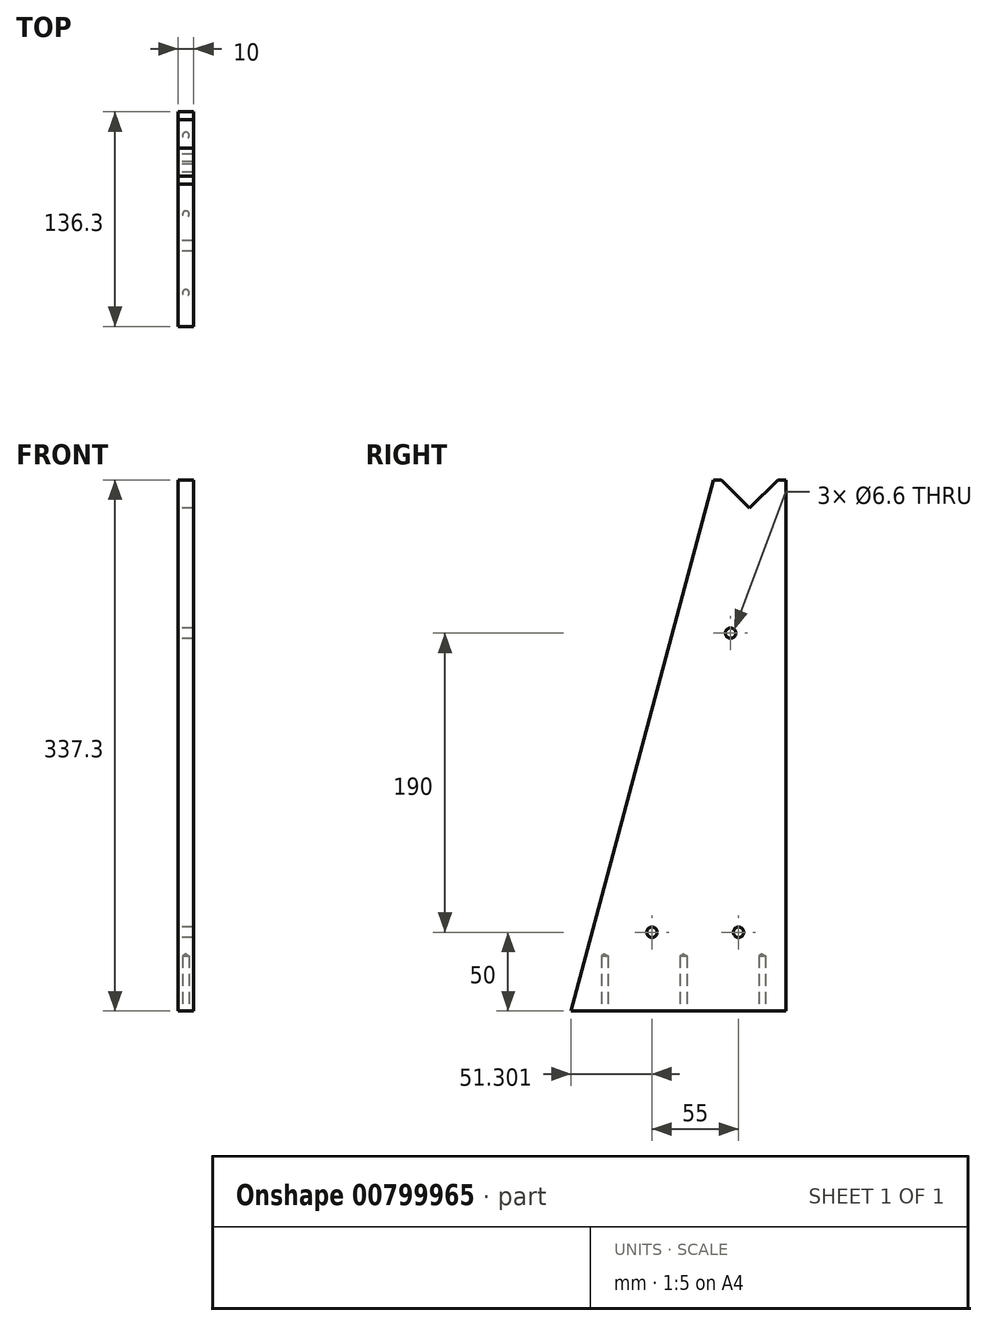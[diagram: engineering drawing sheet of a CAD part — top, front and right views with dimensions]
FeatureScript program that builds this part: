
annotation { "Feature Type Name" : "Feature", "Feature Type Description" : "" }
export const myFeature = defineFeature(function(context is Context, id is Id, definition is map)
    precondition{}
    {
        {
            var Q0;
            Q0=qCreatedBy(makeId("Right.planeOp"),FACE);
            var sketch = newSketch(context, id + "F0", { "sketchPlane" : qUnion([Q0])});
            skLineSegment(sketch, "E0.bottom", {"start": v(-90.9, 0) * mm, "end": v(45.4, 0) * mm});
            skLineSegment(sketch, "E0.right", {"start": v(45.4, 0) * mm, "end": v(45.4, 337.3) * mm});
            skLineSegment(sketch, "E1", {"start": v(22.4, 337.3) * mm, "end": v(22.4, 312.8) * mm, "construction": true});
            skLineSegment(sketch, "E2", {"start": v(22.4, 319.34) * mm, "end": v(4.44, 337.3) * mm});
            skLineSegment(sketch, "E3", {"start": v(22.4, 319.34) * mm, "end": v(40.36, 337.3) * mm});
            skCircle(sketch, "E4", {"center": v(22.4, 337.3) * mm, "radius": 12.7 * mm, "construction": true});
            skPoint(sketch, "E4.first.point", {"position": v(22.4, 350) * mm});
            skPoint(sketch, "E4.second.point", {"position": v(13.42, 328.32) * mm});
            skPoint(sketch, "E4.third.point", {"position": v(31.38, 328.32) * mm});
            skLineSegment(sketch, "E5", {"start": v(-0.52, 337.3) * mm, "end": v(-90.9, 0) * mm});
            skPoint(sketch, "E6.orphan", {"position": v(0, 0) * mm});
            skLineSegment(sketch, "E7", {"start": v(45.4, 337.3) * mm, "end": v(40.36, 337.3) * mm});
            skLineSegment(sketch, "E8", {"start": v(4.44, 337.3) * mm, "end": v(-0.52, 337.3) * mm});
            skSolve(sketch);
        }
        {
            var Q0;
            Q0 = qSketchRegion(id + "F0", true);
            extrude(context, id + "F1", {"entities" : qUnion([Q0]), "depth" : 10 * mm, "offsetDistance" : 25 * mm});
        }
        {
            var Q0;
            Q0=makeQuery(id+"F1.opExtrude","CAP_FACE",FACE,{"disambiguationData":[OSD([sQuery(id+"F0.wireOp",EDGE,"E0.bottom"),sQuery(id+"F0.wireOp",EDGE,"E0.right"),sQuery(id+"F0.wireOp",EDGE,"mPhKqosq-jZKB-q5Nf-kV8y-4qFzDqsdUWAg"),sQuery(id+"F0.wireOp",EDGE,"VODutiJa-ukky-3xt9-Y3hi-ZwQHl53zEOQ1"),sQuery(id+"F0.wireOp",EDGE,"VYFBcTlI-lwus-AauH-xpLd-kEhUKi2z7ShT"),sQuery(id+"F0.wireOp",EDGE,"E2"),sQuery(id+"F0.wireOp",EDGE,"E3")])],"isStart":true});
            var sketch = newSketch(context, id + "F2", { "sketchPlane" : qUnion([Q0])});
            skSolve(sketch);
        }
        {
            var Q0;
            Q0=qCreatedBy(makeId("Right.planeOp"),FACE);
            var sketch = newSketch(context, id + "F3", { "sketchPlane" : qUnion([Q0])});
            skPoint(sketch, "E9", {"position": v(10.4, 240) * mm});
            skPoint(sketch, "E10", {"position": v(15.4, 50) * mm});
            skPoint(sketch, "E11", {"position": v(-39.6, 50) * mm});
            skSolve(sketch);
        }
        {
            var Q0;
            Q0=sQuery(id+"F3.wireOp",VERTEX,"E9");
            var Q1;
            Q1=sQuery(id+"F3.wireOp",VERTEX,"E10");
            var Q2;
            Q2=sQuery(id+"F3.wireOp",VERTEX,"E11");
            var Q3;
            Q3=makeQuery(id+"F1.opExtrude","SWEPT_BODY",BODY,{"disambiguationData":[OSD([sQuery(id+"F0.wireOp",EDGE,"E0.bottom"),sQuery(id+"F0.wireOp",EDGE,"E0.right"),sQuery(id+"F0.wireOp",EDGE,"mPhKqosq-jZKB-q5Nf-kV8y-4qFzDqsdUWAg"),sQuery(id+"F0.wireOp",EDGE,"VODutiJa-ukky-3xt9-Y3hi-ZwQHl53zEOQ1"),sQuery(id+"F0.wireOp",EDGE,"E2"),sQuery(id+"F0.wireOp",EDGE,"E3"),sQuery(id+"F0.wireOp",EDGE,"E5")])]});
            hole(context, id + "F4", {"style" : HoleStyle.SIMPLE, "endStyle" : HoleEndStyle.THROUGH, "oppositeDirection" : true, "standardTappedOrClearance" : lookupTablePath({ "standard" : "ISO", "fit" : "Normal", "size" : "M6", "type" : "Clearance" }), "standardBlindInLast" : lookupTablePath({ "fit" : "Standard", "standard" : "ISO", "size" : "M6", "type" : "Clearance" }), "holeDiameter" : 6.6 * mm, "majorDiameter" : 5 * mm, "isTappedThrough" : true, "tappedDepth" : 12 * mm, "tapClearance" : 3, "locations" : qUnion([Q0, Q1, Q2]), "scope" : qUnion([Q3])});
        }
        {
            var Q0;
            Q0=makeQuery(id+"F1.opExtrude","SWEPT_FACE",FACE,{"disambiguationData":[OSD([sQuery(id+"F0.wireOp",EDGE,"E0.bottom")])]});
            var sketch = newSketch(context, id + "F5", { "sketchPlane" : qUnion([Q0])});
            skLineSegment(sketch, "E12", {"start": v(5, 90.9) * mm, "end": v(5, -45.4) * mm, "construction": true});
            skPoint(sketch, "E13", {"position": v(5, 69.6) * mm});
            skPoint(sketch, "E14", {"position": v(5, -30.4) * mm});
            skPoint(sketch, "E15", {"position": v(5, 19.6) * mm});
            skSolve(sketch);
        }
        {
            var Q0;
            Q0=sQuery(id+"F5.wireOp",VERTEX,"E13");
            var Q1;
            Q1=sQuery(id+"F5.wireOp",VERTEX,"E15");
            var Q2;
            Q2=sQuery(id+"F5.wireOp",VERTEX,"E14");
            var Q3;
            Q3=makeQuery(id+"F1.opExtrude","SWEPT_BODY",BODY,{"disambiguationData":[OSD([sQuery(id+"F0.wireOp",EDGE,"E0.bottom"),sQuery(id+"F0.wireOp",EDGE,"E0.right"),sQuery(id+"F0.wireOp",EDGE,"mPhKqosq-jZKB-q5Nf-kV8y-4qFzDqsdUWAg"),sQuery(id+"F0.wireOp",EDGE,"VODutiJa-ukky-3xt9-Y3hi-ZwQHl53zEOQ1"),sQuery(id+"F0.wireOp",EDGE,"E2"),sQuery(id+"F0.wireOp",EDGE,"E3"),sQuery(id+"F0.wireOp",EDGE,"E5")])]});
            hole(context, id + "F6", {"style" : HoleStyle.SIMPLE, "endStyle" : HoleEndStyle.BLIND, "standardTappedOrClearance" : lookupTablePath({ "standard" : "ISO", "engagement" : "75%", "pitch" : "0.8 mm", "size" : "M5", "type" : "Tapped" }), "standardBlindInLast" : lookupTablePath({ "standard" : "ISO", "engagement" : "75%", "pitch" : "0.8 mm", "size" : "M5", "type" : "Tapped" }), "holeDiameter" : 4.2 * mm, "majorDiameter" : 5 * mm, "showTappedDepth" : true, "holeDepth" : 35 * mm, "isTappedThrough" : true, "tappedDepth" : 32.6 * mm, "tapClearance" : 3, "locations" : qUnion([Q0, Q1, Q2]), "scope" : qUnion([Q3])});
        }
    });
